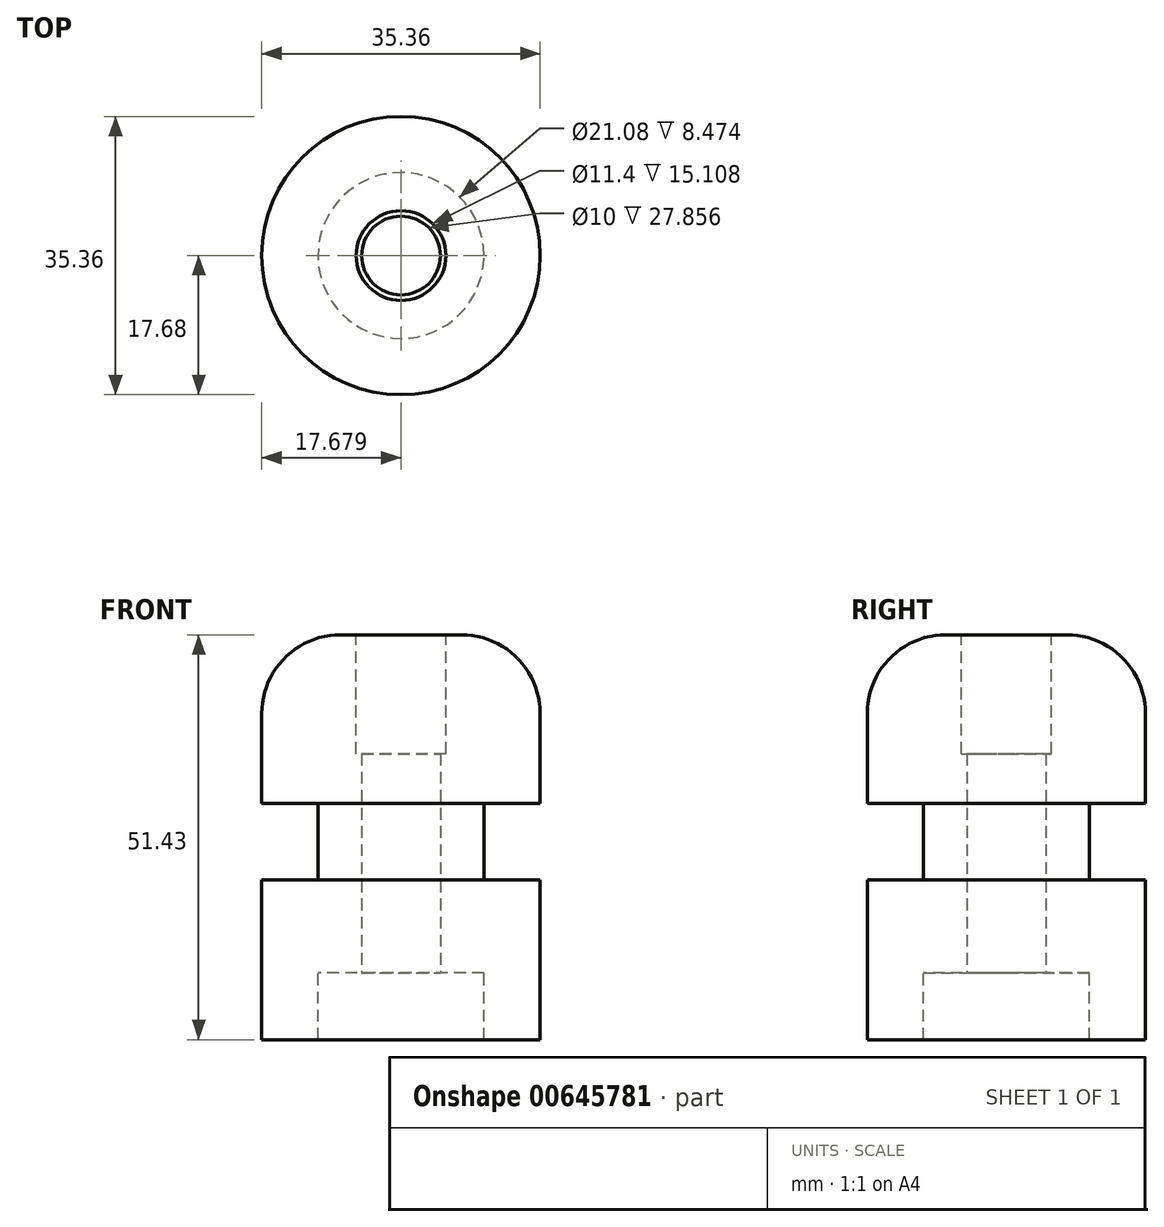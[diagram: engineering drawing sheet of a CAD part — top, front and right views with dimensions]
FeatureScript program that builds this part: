
annotation { "Feature Type Name" : "Feature", "Feature Type Description" : "" }
export const myFeature = defineFeature(function(context is Context, id is Id, definition is map)
    precondition{}
    {
        {
            var Q0;
            Q0=qCreatedBy(makeId("Front.planeOp"),FACE);
            var sketch = newSketch(context, id + "F0", { "sketchPlane" : qUnion([Q0])});
            skLineSegment(sketch, "E0", {"start": v(-4.84, 42.96) * mm, "end": v(7.14, 42.96) * mm});
            skLineSegment(sketch, "E1", {"start": v(7.14, 42.96) * mm, "end": v(7.14, 21.52) * mm});
            skLineSegment(sketch, "E2", {"start": v(7.14, -8.47) * mm, "end": v(0, -8.47) * mm});
            skLineSegment(sketch, "E3", {"start": v(0, -8.47) * mm, "end": v(0, 0) * mm});
            skLineSegment(sketch, "E4", {"start": v(-10.54, 54.83) * mm, "end": v(-10.54, -22.57) * mm});
            skLineSegment(sketch, "E5", {"start": v(0, 0) * mm, "end": v(-10.54, 0) * mm});
            skLineSegment(sketch, "E6", {"start": v(-4.84, 42.96) * mm, "end": v(-4.84, 27.86) * mm});
            skLineSegment(sketch, "E7", {"start": v(-4.84, 27.86) * mm, "end": v(-10.54, 27.86) * mm});
            skLineSegment(sketch, "E8", {"start": v(7.14, 21.52) * mm, "end": v(0, 21.52) * mm});
            skLineSegment(sketch, "E9", {"start": v(0, 21.52) * mm, "end": v(0, 11.84) * mm});
            skLineSegment(sketch, "E10", {"start": v(0, 11.84) * mm, "end": v(7.14, 11.84) * mm});
            skLineSegment(sketch, "E11.trimOffspring", {"start": v(7.14, 11.84) * mm, "end": v(7.14, -8.47) * mm});
            skSolve(sketch);
        }
        {
            var Q0;
            Q0 = qSketchRegion(id + "F0", true);
            var Q1;
            Q1=sQuery(id+"F0.wireOp",EDGE,"E4");
            revolve(context, id + "F1", {"entities" : qUnion([Q0]), "axis" : qUnion([Q1]), "revolveType" : RevolveType.FULL});
        }
        {
            var Q0;
            Q0=makeQuery(id+"F1.opRevolve","SWEPT_FACE",FACE,{"disambiguationData":[OSD([sQuery(id+"F0.wireOp",EDGE,"E5")])]});
            var sketch = newSketch(context, id + "F2", { "sketchPlane" : qUnion([Q0])});
            skCircle(sketch, "E12", {"center": v(-10.54, 0) * mm, "radius": 3.8 * mm});
            skSolve(sketch);
        }
        {
            var Q0;
            Q0=sQuery(id+"F2.wireOp",VERTEX,"E12.center");
            var Q1;
            Q1=makeQuery(id+"F1.opRevolve","SWEPT_BODY",BODY,{"disambiguationData":[OSD([sQuery(id+"F0.wireOp",EDGE,"E0"),sQuery(id+"F0.wireOp",EDGE,"E1"),sQuery(id+"F0.wireOp",EDGE,"E2"),sQuery(id+"F0.wireOp",EDGE,"E3"),sQuery(id+"F0.wireOp",EDGE,"E4"),sQuery(id+"F0.wireOp",EDGE,"E5"),sQuery(id+"F0.wireOp",EDGE,"E6"),sQuery(id+"F0.wireOp",EDGE,"E7"),sQuery(id+"F0.wireOp",EDGE,"E8"),sQuery(id+"F0.wireOp",EDGE,"E9"),sQuery(id+"F0.wireOp",EDGE,"E10"),sQuery(id+"F0.wireOp",EDGE,"E11.trimOffspring")])]});
            hole(context, id + "F3", {"style" : HoleStyle.SIMPLE, "endStyle" : HoleEndStyle.THROUGH, "holeDiameter" : 10 * mm, "majorDiameter" : 5 * mm, "isTappedThrough" : true, "tappedDepth" : 12 * mm, "tapClearance" : 3, "locations" : qUnion([Q0]), "scope" : qUnion([Q1])});
        }
        {
            var Q0;
            Q0=makeQuery(id+"F1.opRevolve","SWEPT_EDGE",EDGE,{"disambiguationData":[OSD([sQuery(id+"F0.wireOp",EDGE,"E0"),sQuery(id+"F0.wireOp",EDGE,"E1")])]});
            fillet(context, id + "F4", {"entities" : qUnion([Q0]), "radius" : 10 * mm, "tangentPropagation" : true, "allowEdgeOverflow" : false});
        }
    });
